# Revit family: FantiniCosmi_BIM_CH119NFC
name_source: partatom
category: Generic Models
units: mm (PartAtom-declared; Revit-internal decimal feet)

## family parameters
Always vertical = Yes
Can host rebar = No
Cut with Voids When Loaded = No
Part Type = Normal
Room Calculation Point = No
Round Connector Dimension = Use Diameter
Shared = No
Work Plane-Based = No

## types (1)
- Standard
    Catalog web link = https://www.fantinicosmi.it
    Default Elevation = 0 mm  [stored 0 ft]
    Description = Electronic room thermostat with batteries, 3 temperature levels
    Differential = 0.3 ÷ 5 K
    Dimensions = 135 x 83 x 21mm
    Electric insulation = Double insulation
    Maximum ambient temperature = 45 °C
    Micro disconnection = 1B
    Output type = 1 relay for heating and cooling systems (3 screw clamps (closed + open)
    Part Number = CH119NFC
    Power supply = 2 batteries AA
    Protection degree = IP20
    Pulse voltage = 4000V
    Software Class = A
    Temperature regulation range = 2 ÷ 40 °C
    Type of action = 1 B.U. (connection micro-switch)

note: [stored X ft] marks values corroborated as IEEE doubles in the binary element streams (Revit-internal decimal feet)

## geometry (parser evidence)
native form markers: Sweep x3
no freeform markers — native parametric forms only
